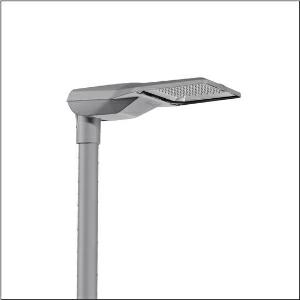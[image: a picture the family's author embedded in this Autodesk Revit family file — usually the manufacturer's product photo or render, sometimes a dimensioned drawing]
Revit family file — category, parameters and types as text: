
# Revit family: streetlight_sl_21_midi___stw1_0a_5xe7e23a08lb_d37f
name_source: partatom
category: Lighting Fixtures
units: mm (PartAtom-declared; Revit-internal decimal feet)

## family parameters
Cut with Voids When Loaded = No
Host = Face
Light Source = No
Part Type = Normal
Room Calculation Point = No
Round Connector Dimension = Use Diameter
Shared = No

## types (1)
- --- (1 x LED, 11880 lm, 98.3 W, 2200K)
    Apparent Load = 98 VA
    CIE Flux Codes = 38 75 98 100 100
    Color Rendering = 70
    Color Temperature = 2200K
    Default Elevation = 1800 mm
    Description = Streetlight SL 21 midi, mast luminaire, primary light control with lens, of PMMA, primary optical cover: cover, of toughened safety glass, transparent, light distribution: STW1.0a, light emission: direct distribution, primary light characteristic: asymmetric, installation type: post-top, side-entry, LED, 3G 1.5mm², High Power LED, rated luminous flux: 11.880lm, luminous efficacy: 121lm/W, light colour: 722, colour temperature: 2200K, control: overheat protection, constant luminous flux control, time-dependent luminous flux control, flexible luminous flux parameterisation, mains connection: 220..240V, AC, 50/60Hz, connection cable pre-assembled, cable length: 10,5m, wiring characteristics: H07RN-F, start of lifetime: 98W, end of service life: 101W, reduction: 44W, luminaire housing, of diecast aluminium, powder-coated, Siteco® metallic grey (DB 702S), corrosivity category C5 mid according to DIN EN ISO 12944, please order mast flange separately, inclination adjustable: 0°, 5°, 10°, 15°, sealing non-destructively replaceable, multi-level sealing system, length: 644mm, width: 335mm, height: 110mm, mast flange for spigot size: 42mm (side-entry): 5XC10008XM4, 60/48mm (side-entry/post-top): 5XC10108XM2, 76/60mm (side-entry/post-top): 5XC10108XM1, protection rating (complete): IP66, insulation class (complete): insulation class II (safety insulation), certification: CE, ENEC, ENEC+, VDE, impact resistance: IK09, permissible operating ambient temperature for outdoor applications: -40..+50°C, standard-compliant lighting for roads and squares, packaging unit: 1 piece

Light Distribution: STW1.0a
    Height = 111 mm
    Lamp = 1 x LED
    Lamp Light Flux = 11880 lm
    Lamp Power = 98.3 W
    Lamp count = 1
    Length = 644 mm
    Luminous efficacy = 121 lm/W
    Manufacturer = Siteco
    ModVariant = No
    Model = 5XE7E23A08LB
    Number of Poles = 1
    OnlyDefault = Yes
    Power Factor = 1
    Product Name = Streetlight SL 21 midi | STW1.0a
    Product group = mast luminaire | pylon top
    ProductGroupID = 6100
    Protection Class = Protection class II
    Protection Degree = IP 66
    RLX_Detail_Level = 1
    RLX_Emergency_Light_Flux = 0 lm
    RLX_Emergency_Type = 0
    RLX_Emergency_Type_DB = No
    RlxData = <blob elided: 90241 chars, md5=6ba02e15>
    Socket = socket
    Standby Power = 0 W
    System Light Flux = 11880 lm
    System Power = 98 W
    Type Comments = factory setting: luminous flux: 100 % | Output Level: 100 % | 1020 mA
    Type Image = l_1004298.jpg
    URL = http://relux.com
    VarID = @adj_139661
    Voltage = 0 V
    Weight = 0.00 kg
    Width = 336 mm

## geometry (parser evidence)
native form markers: Blend x4, Sweep x11
no freeform markers — native parametric forms only
